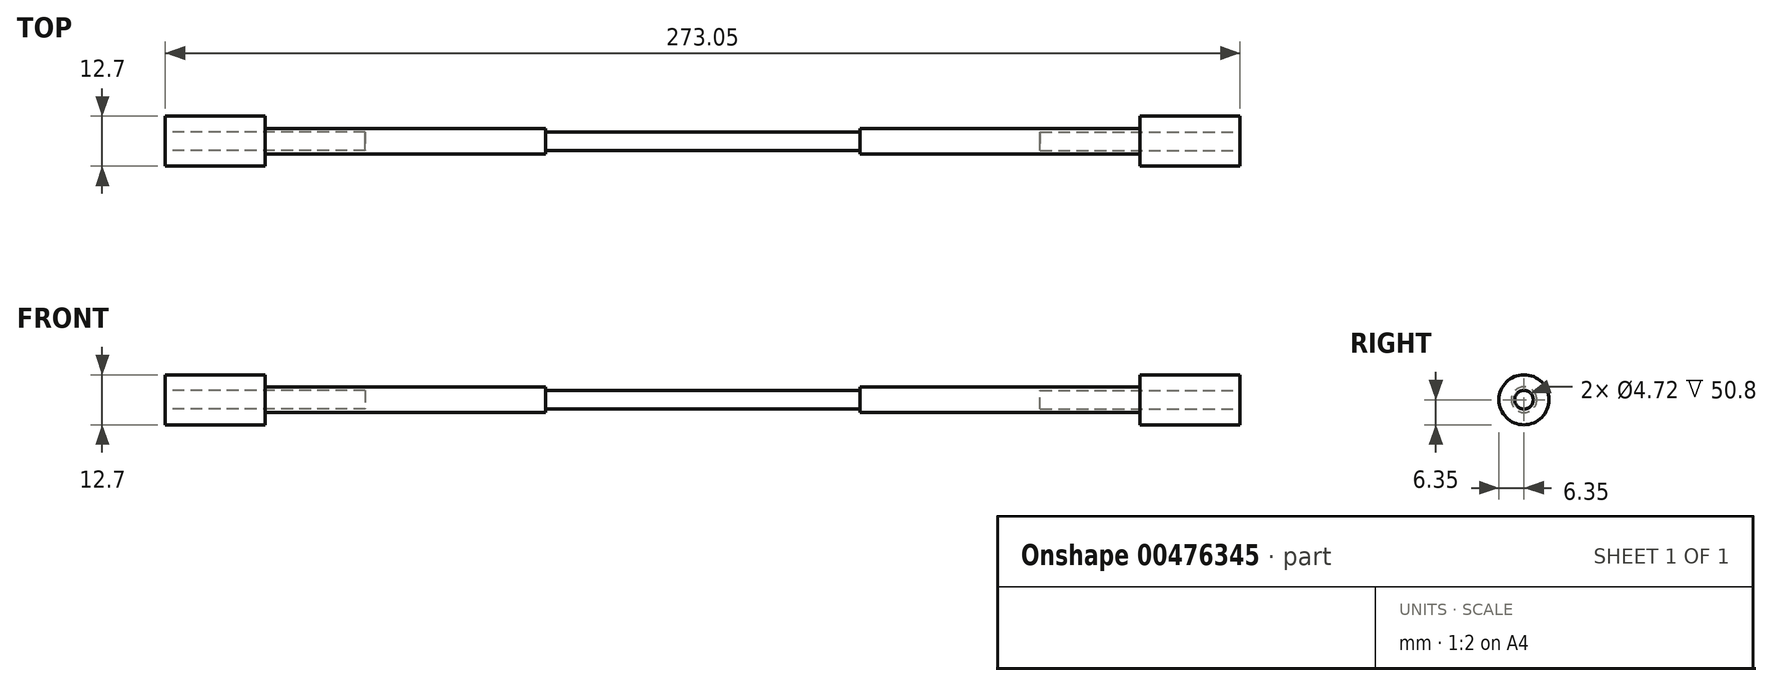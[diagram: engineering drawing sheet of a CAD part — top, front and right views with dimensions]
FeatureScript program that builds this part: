
annotation { "Feature Type Name" : "Feature", "Feature Type Description" : "" }
export const myFeature = defineFeature(function(context is Context, id is Id, definition is map)
    precondition{}
    {
        {
            var Q0;
            Q0=qCreatedBy(makeId("Right.planeOp"),FACE);
            var sketch = newSketch(context, id + "F0", { "sketchPlane" : qUnion([Q0])});
            skCircle(sketch, "E0", {"center": v(0, 0) * mm, "radius": 2.36 * mm});
            skSolve(sketch);
        }
        {
            var Q0;
            Q0=makeQuery(id+"F0.imprint","IMPRINT",FACE,{"disambiguationData":[TD([[makeQuery(id+"F0.imprint","IMPRINT",EDGE,{"derivedFrom":sQuery(id+"F0.wireOp",EDGE,"E0")}),1.0]])]});
            var Q1;
            Q1=sQuery(id+"F0.wireOp",EDGE,"E0");
            extrude(context, id + "F1", {"entities" : qUnion([Q0]), "surfaceEntities" : qUnion([Q1]), "depth" : 105.4 * mm});
        }
        {
            var Q0;
            Q0=qCreatedBy(makeId("Right.planeOp"),FACE);
            cPlane(context, id + "F2", {"entities" : qUnion([Q0]), "cplaneType" : CPlaneType.OFFSET, "offset" : 12.7 * mm, "width" : 152.4 * mm, "height" : 152.4 * mm});
        }
        {
            var Q0;
            Q0=qCreatedBy(id+"F2.planeOp",FACE);
            var sketch = newSketch(context, id + "F3", { "sketchPlane" : qUnion([Q0])});
            skCircle(sketch, "E1", {"center": v(0, 0) * mm, "radius": 3.25 * mm});
            skSolve(sketch);
        }
        {
            var Q0;
            Q0 = qSketchRegion(id + "F3", true);
            extrude(context, id + "F4", {"entities" : qUnion([Q0]), "operationType" : NewBodyOperationType.ADD, "oppositeDirection" : true, "depth" : 96.53 * mm});
        }
        {
            var Q0;
            Q0=qCreatedBy(id+"F2.planeOp",FACE);
            cPlane(context, id + "F5", {"entities" : qUnion([Q0]), "cplaneType" : CPlaneType.OFFSET, "offset" : 80 * mm, "width" : 152.4 * mm, "height" : 152.4 * mm});
        }
        {
            var Q0;
            Q0=qCreatedBy(id+"F5.planeOp",FACE);
            var sketch = newSketch(context, id + "F6", { "sketchPlane" : qUnion([Q0])});
            skCircle(sketch, "E2", {"center": v(0, 0) * mm, "radius": 3.25 * mm});
            skSolve(sketch);
        }
        {
            var Q0;
            Q0 = qSketchRegion(id + "F6", true);
            extrude(context, id + "F7", {"entities" : qUnion([Q0]), "operationType" : NewBodyOperationType.ADD, "depth" : 96.53 * mm});
        }
        {
            var Q0;
            Q0=makeQuery(id+"F4.opExtrude","CAP_FACE",FACE,{"disambiguationData":[OSD([sQuery(id+"F3.wireOp",EDGE,"E1")])],"isStart":false});
            var sketch = newSketch(context, id + "F8", { "sketchPlane" : qUnion([Q0])});
            skCircle(sketch, "E3", {"center": v(0, 0) * mm, "radius": 6.35 * mm});
            skSolve(sketch);
        }
        {
            var Q0;
            Q0=makeQuery(id+"F8.imprint","IMPRINT",FACE,{"disambiguationData":[TD([[makeQuery(id+"F8.imprint","IMPRINT",EDGE,{"derivedFrom":sQuery(id+"F8.wireOp",EDGE,"E3")}),1.0]])]});
            var Q1;
            Q1=sQuery(id+"F8.wireOp",EDGE,"E3");
            extrude(context, id + "F9", {"entities" : qUnion([Q0]), "operationType" : NewBodyOperationType.ADD, "surfaceEntities" : qUnion([Q1]), "oppositeDirection" : true, "depth" : 25.4 * mm});
        }
        {
            var Q0;
            Q0=makeQuery(id+"F4.opExtrude","CAP_FACE",FACE,{"disambiguationData":[OSD([sQuery(id+"F3.wireOp",EDGE,"E1")])],"isStart":false});
            var sketch = newSketch(context, id + "F10", { "sketchPlane" : qUnion([Q0])});
            skCircle(sketch, "E4", {"center": v(0, 0) * mm, "radius": 2.36 * mm});
            skSolve(sketch);
        }
        {
            var Q0;
            Q0 = qSketchRegion(id + "F10", true);
            extrude(context, id + "F11", {"entities" : qUnion([Q0]), "operationType" : NewBodyOperationType.REMOVE, "oppositeDirection" : true, "depth" : 50.8 * mm});
        }
        {
            var Q0;
            Q0=makeQuery(id+"F7.opExtrude","CAP_FACE",FACE,{"disambiguationData":[OSD([sQuery(id+"F6.wireOp",EDGE,"E2")])],"isStart":false});
            var sketch = newSketch(context, id + "F12", { "sketchPlane" : qUnion([Q0])});
            skCircle(sketch, "E5", {"center": v(0, 0) * mm, "radius": 6.35 * mm});
            skSolve(sketch);
        }
        {
            var Q0;
            Q0=makeQuery(id+"F12.imprint","IMPRINT",FACE,{"disambiguationData":[TD([[makeQuery(id+"F12.imprint","IMPRINT",EDGE,{"derivedFrom":sQuery(id+"F12.wireOp",EDGE,"E5")}),1.0]])]});
            var Q1;
            Q1=sQuery(id+"F12.wireOp",EDGE,"E5");
            extrude(context, id + "F13", {"entities" : qUnion([Q0]), "operationType" : NewBodyOperationType.ADD, "surfaceEntities" : qUnion([Q1]), "oppositeDirection" : true, "depth" : 25.4 * mm});
        }
        {
            var Q0;
            Q0=makeQuery(id+"F7.opExtrude","CAP_FACE",FACE,{"disambiguationData":[OSD([sQuery(id+"F6.wireOp",EDGE,"E2")])],"isStart":false});
            var sketch = newSketch(context, id + "F14", { "sketchPlane" : qUnion([Q0])});
            skCircle(sketch, "E6", {"center": v(0, 0) * mm, "radius": 2.36 * mm});
            skSolve(sketch);
        }
        {
            var Q0;
            Q0 = qSketchRegion(id + "F14", true);
            extrude(context, id + "F15", {"entities" : qUnion([Q0]), "operationType" : NewBodyOperationType.REMOVE, "oppositeDirection" : true, "depth" : 50.8 * mm});
        }
    });
